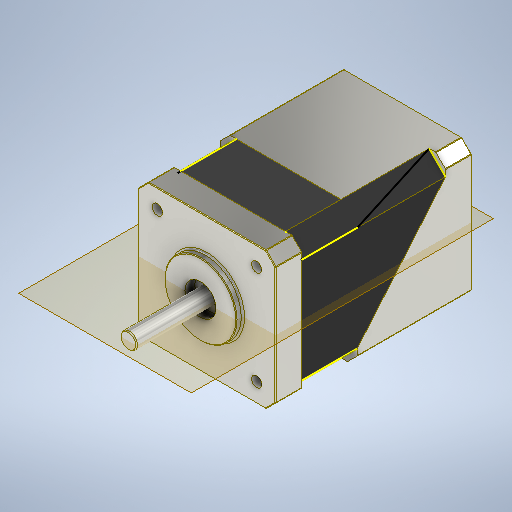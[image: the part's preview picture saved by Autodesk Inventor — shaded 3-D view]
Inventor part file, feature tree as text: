
AUTODESK INVENTOR PART (.ipt)
format: ipt  version: 2025 (Build 290162000, 162)  size: 712,192 bytes
history: native  units: mm
features: extrude x19, chamfer x12, fillet x7, sketch x6, thread x4, plane x1
ambient origin geometry x8: Origin, YZ Plane, XZ Plane, XY Plane, X Axis, Y Axis, Z Axis, Center Point
bodies: Solid1 (feature_tree)
feature tree (49):
  extrude  "Extrusion1"  Depth=42.0mm
  chamfer  "Chamfer6"  Distance=60.0mm
  chamfer  "Chamfer7"  Distance=3.0mm Angle=45.0deg
  chamfer  "Chamfer8"  Distance=3.0mm Angle=45.0deg
  chamfer  "Chamfer9"  Distance=3.0mm Angle=45.0deg
  chamfer  "Chamfer10"  Distance=35.0mm
  chamfer  "Chamfer11"  Distance=3.0mm Angle=45.0deg
  chamfer  "Chamfer12"  Distance=3.0mm Angle=45.0deg
  chamfer  "Chamfer13"  Distance=35.0mm
  chamfer  "Chamfer14"  Distance=5.0mm Angle=45.0deg
  chamfer  "Chamfer15"  Distance=16.989mm
  chamfer  "Chamfer16"  Distance=3.0mm Angle=45.0deg
  chamfer  "Chamfer17"  Distance=3.0mm Angle=45.0deg
  extrude  "Extrusion3"  Depth=3.0mm TaperAngle=45.0deg
  extrude  "Extrusion4"  Depth=0.01mm TaperAngle=0.0deg
  extrude  "Extrusion5"  Depth=0.01mm TaperAngle=0.0deg
  extrude  "Extrusion6"  Depth=0.01mm TaperAngle=0.0deg
  extrude  "Extrusion7"  Depth=0.01mm TaperAngle=0.0deg
  extrude  "Extrusion8"  Depth=22.0mm
  extrude  "Extrusion9"  Depth=2.0mm TaperAngle=0.0deg
  extrude  "Extrusion10"  Depth=9.5mm
  extrude  "Extrusion11"  Depth=3.0mm TaperAngle=0.0deg
  fillet  "Fillet1"  Radius=5.0mm
  extrude  "Extrusion12"  Depth=25.0mm TaperAngle=0.0deg
  thread  "Thread1"  [1 undecoded]
  thread  "Thread2"  [1 undecoded]
  thread  "Thread3"  [1 undecoded]
  thread  "Thread4"  [1 undecoded]
  extrude  "Extrusion13"  Depth=5.8mm
  extrude  "Extrusion14"  Depth=5.8mm
  extrude  "Extrusion15"  Depth=3.2mm
  fillet  "Fillet2"  Radius=5.8mm
  fillet  "Fillet3"  Radius=5.8mm
  extrude  "Extrusion16"  Depth=3.1mm
  extrude  "Extrusion17"  Depth=5.8mm
  extrude  "Extrusion18"  Depth=5.8mm
  extrude  "Extrusion19"  Depth=3.1mm
  extrude  "Extrusion20"  Depth=5.8mm
  fillet  "Fillet4"  Radius=5.8mm
  fillet  "Fillet5"  Radius=3.1mm
  fillet  "Fillet6"  Radius=50.0mm
  fillet  "Fillet8"  Radius=4.0mm
  plane  "Work Plane1"
  sketch  "Sketch10"  dims[d0=42.0mm d1=42.0mm d2=60.0mm d3=0.0mm]
  sketch  "Sketch23"  dims[d32=5.0mm d33=2.0mm d34=45.0deg d35=8.0mm d36=44.0mm d37=8.0mm d38=3.0mm d39=2.0mm d40=45.0deg d41=3.0mm d42=2.0mm d43=45.0deg d44=3.0mm d45=2.0mm d46=45.0deg d47=0.0mm d48=35.0mm d49=25.0mm]
  sketch  "Sketch27"  dims[d50=5.0mm d51=2.0mm d52=45.0deg d53=0.002mm d54=16.998mm d55=8.0mm d56=3.0mm d57=2.0mm d58=45.0deg d59=3.0mm d60=2.0mm d61=45.0deg d62=0.0mm d63=35.0mm d64=25.0mm d65=5.0mm d66=2.0mm d67=45.0deg d68=0.011mm d69=16.989mm d70=8.0mm d71=3.0mm d72=2.0mm d73=45.0deg d74=3.0mm d75=2.0mm d76=45.0deg]
  sketch  "Sketch32"  dims[d77=0.0mm d78=35.0mm d79=25.0mm]
  sketch  "Sketch35"  dims[d80=5.0mm d81=2.0mm d82=45.0deg d83=0.015mm d84=16.985mm d85=8.0mm d86=3.0mm d87=2.0mm d88=45.0deg]
  sketch  "Sketch36"  dims[d89=8.0mm d90=0.0mm d91=0.01mm d92=0.0mm d93=0.01mm d94=0.0mm d95=0.01mm d96=0.0mm d97=0.01mm d98=0.0mm d99=22.0mm d100=2.0mm d101=0.0mm d102=9.5mm d103=3.0mm d104=0.0mm d105=5.0mm d106=25.0mm d107=0.0mm d108=15.0mm d109=4.5mm d110=25.0mm d111=0.0mm d112=0.25mm d113=5.8mm d114=5.8mm d115=3.2mm d116=5.8mm d117=5.8mm d118=3.1mm d119=5.8mm d120=5.8mm d121=3.1mm d122=5.8mm d123=5.8mm d124=3.1mm d125=50.0mm d126=0.0mm d127=4.0mm d128=0.0mm d129=4.0mm d130=0.0mm d131=50.0mm d132=0.0mm d133=4.0mm d134=0.0mm d135=7.0mm d136=4.0mm d137=0.0mm d138=5.8mm d139=5.8mm d140=5.8mm d141=5.8mm d142=2.5mm d143=0.0mm d144=16.0mm d145=8.0mm d146=2.0mm d147=4.3mm d148=0.0mm d149=0.5mm d150=0.2mm d151=5.5mm d152=15.0mm d153=0.5mm d154=6.0mm d155=0.0mm d156=3.9mm d157=13.0mm d158=1.0mm d159=4.5mm d160=0.0mm d161=7.8mm d162=3.9mm d163=4.5mm d164=0.0mm d165=4.0mm d166=1.0mm d167=1.0mm d168=1.0mm d169=1.0mm d170=0.84mm d171=0.0mm d172=0.5mm d173=0.5mm d174=0.5mm d175=1.6mm d176=0.5mm d177=0.5mm d178=0.5mm d179=0.5mm d180=1.6mm d181=1.6mm d182=1.6mm d184=1.6mm d185=1.0mm d186=1.0mm d187=4.0mm d188=0.0mm d189=0.2mm d190=0.3mm d191=0.3mm d193=0.05mm d194=0.0mm d196=0.5mm d197=0.5mm d198=0.0mm d195=0.872665mm]
note: 4 required parameter values undecoded (feature->parameter linkage not recoverable at this tier; creation-order binding heuristic only, values carry confidence <= 0.55)
